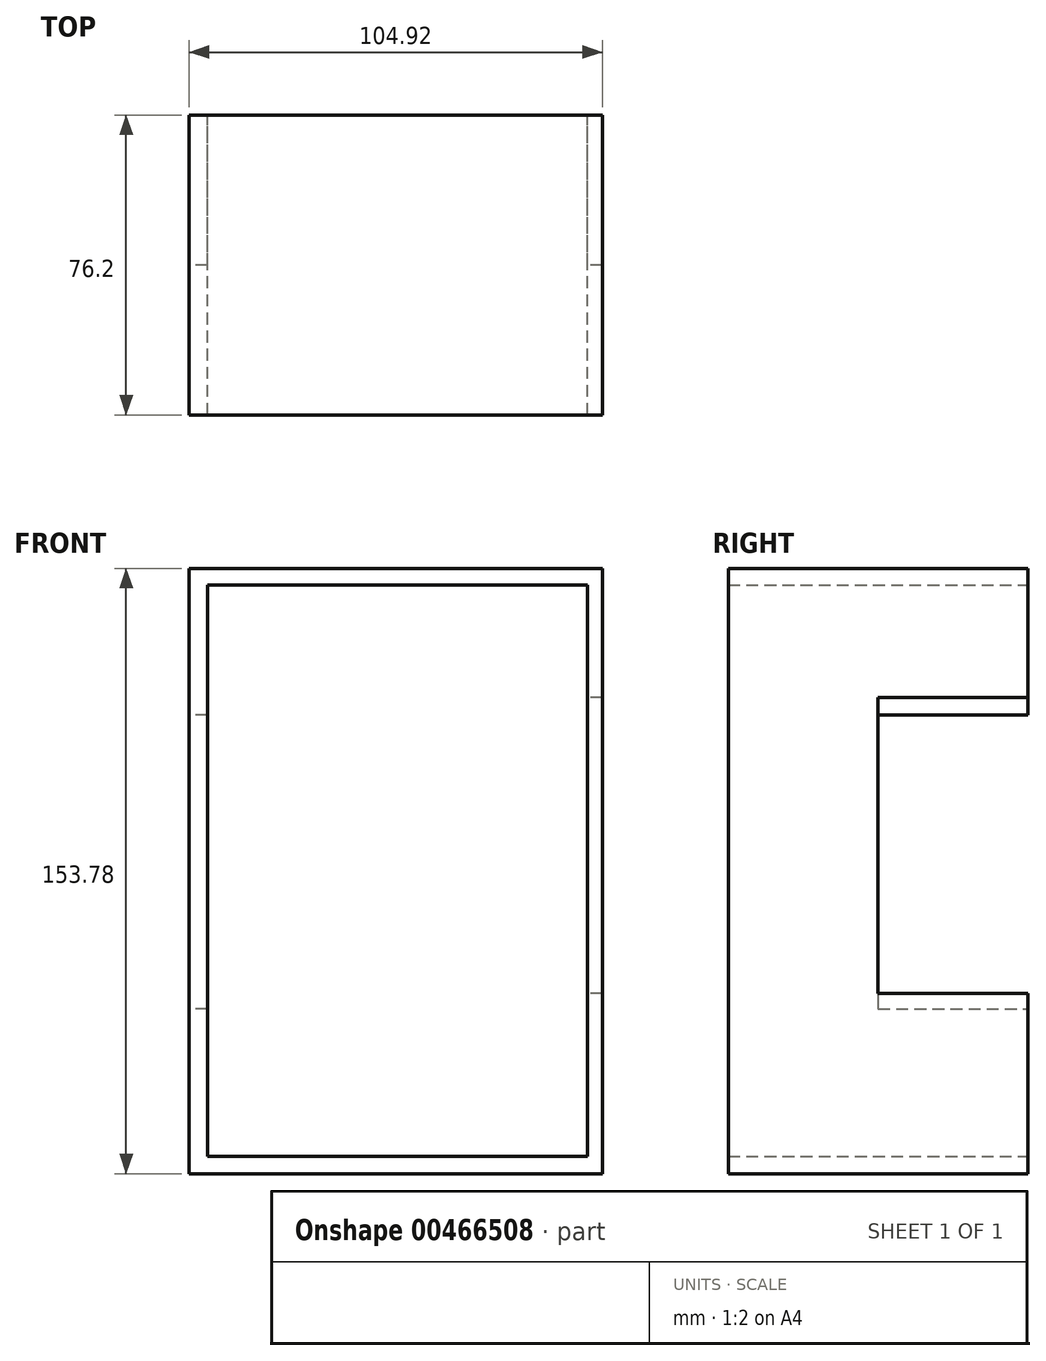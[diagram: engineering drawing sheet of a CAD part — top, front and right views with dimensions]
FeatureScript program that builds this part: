
annotation { "Feature Type Name" : "Feature", "Feature Type Description" : "" }
export const myFeature = defineFeature(function(context is Context, id is Id, definition is map)
    precondition{}
    {
        {
            var Q0;
            Q0=qCreatedBy(makeId("Front.planeOp"),FACE);
            var sketch = newSketch(context, id + "F0", { "sketchPlane" : qUnion([Q0])});
            skLineSegment(sketch, "E0.bottom", {"start": v(-70.42, 77.42) * mm, "end": v(34.5, 77.42) * mm});
            skLineSegment(sketch, "E0.top", {"start": v(-70.42, -76.36) * mm, "end": v(34.5, -76.36) * mm});
            skLineSegment(sketch, "E0.left", {"start": v(-70.42, 77.42) * mm, "end": v(-70.42, -76.36) * mm});
            skLineSegment(sketch, "E0.right", {"start": v(34.5, 77.42) * mm, "end": v(34.5, -76.36) * mm});
            skLineSegment(sketch, "E1.bottom", {"start": v(-65.8, 73.18) * mm, "end": v(30.74, 73.18) * mm});
            skLineSegment(sketch, "E1.top", {"start": v(-65.8, -71.98) * mm, "end": v(30.74, -71.98) * mm});
            skLineSegment(sketch, "E1.left", {"start": v(-65.8, 73.18) * mm, "end": v(-65.8, -71.98) * mm});
            skLineSegment(sketch, "E1.right", {"start": v(30.74, 73.18) * mm, "end": v(30.74, -71.98) * mm});
            skSolve(sketch);
        }
        {
            var Q0;
            Q0=makeQuery(id+"F0.imprint","IMPRINT",FACE,{"disambiguationData":[TD([[makeQuery(id+"F0.imprint","IMPRINT",EDGE,{"derivedFrom":sQuery(id+"F0.wireOp",EDGE,"E0.bottom")}),-1.0]])]});
            extrude(context, id + "F1", {"entities" : qUnion([Q0]), "depth" : 76.2 * mm});
        }
        {
            var Q0;
            Q0=qCreatedBy(makeId("Front.planeOp"),FACE);
            var sketch = newSketch(context, id + "F2", { "sketchPlane" : qUnion([Q0])});
            skLineSegment(sketch, "E2.bottom", {"start": v(39.9, -30.57) * mm, "end": v(24.53, -30.57) * mm});
            skLineSegment(sketch, "E2.top", {"start": v(39.9, 44.6) * mm, "end": v(24.53, 44.6) * mm});
            skLineSegment(sketch, "E2.left", {"start": v(39.9, -30.57) * mm, "end": v(39.9, 44.6) * mm});
            skLineSegment(sketch, "E2.right", {"start": v(24.53, -30.57) * mm, "end": v(24.53, 44.6) * mm});
            skLineSegment(sketch, "E3.bottom", {"start": v(-63.13, 40.22) * mm, "end": v(-76.53, 40.22) * mm});
            skLineSegment(sketch, "E3.top", {"start": v(-63.13, -34.51) * mm, "end": v(-76.53, -34.51) * mm});
            skLineSegment(sketch, "E3.left", {"start": v(-63.13, 40.22) * mm, "end": v(-63.13, -34.51) * mm});
            skLineSegment(sketch, "E3.right", {"start": v(-76.53, 40.22) * mm, "end": v(-76.53, -34.51) * mm});
            skSolve(sketch);
        }
        {
            var Q0;
            Q0 = qSketchRegion(id + "F2", true);
            extrude(context, id + "F3", {"entities" : qUnion([Q0]), "operationType" : NewBodyOperationType.REMOVE, "depth" : 38.1 * mm});
        }
    });
